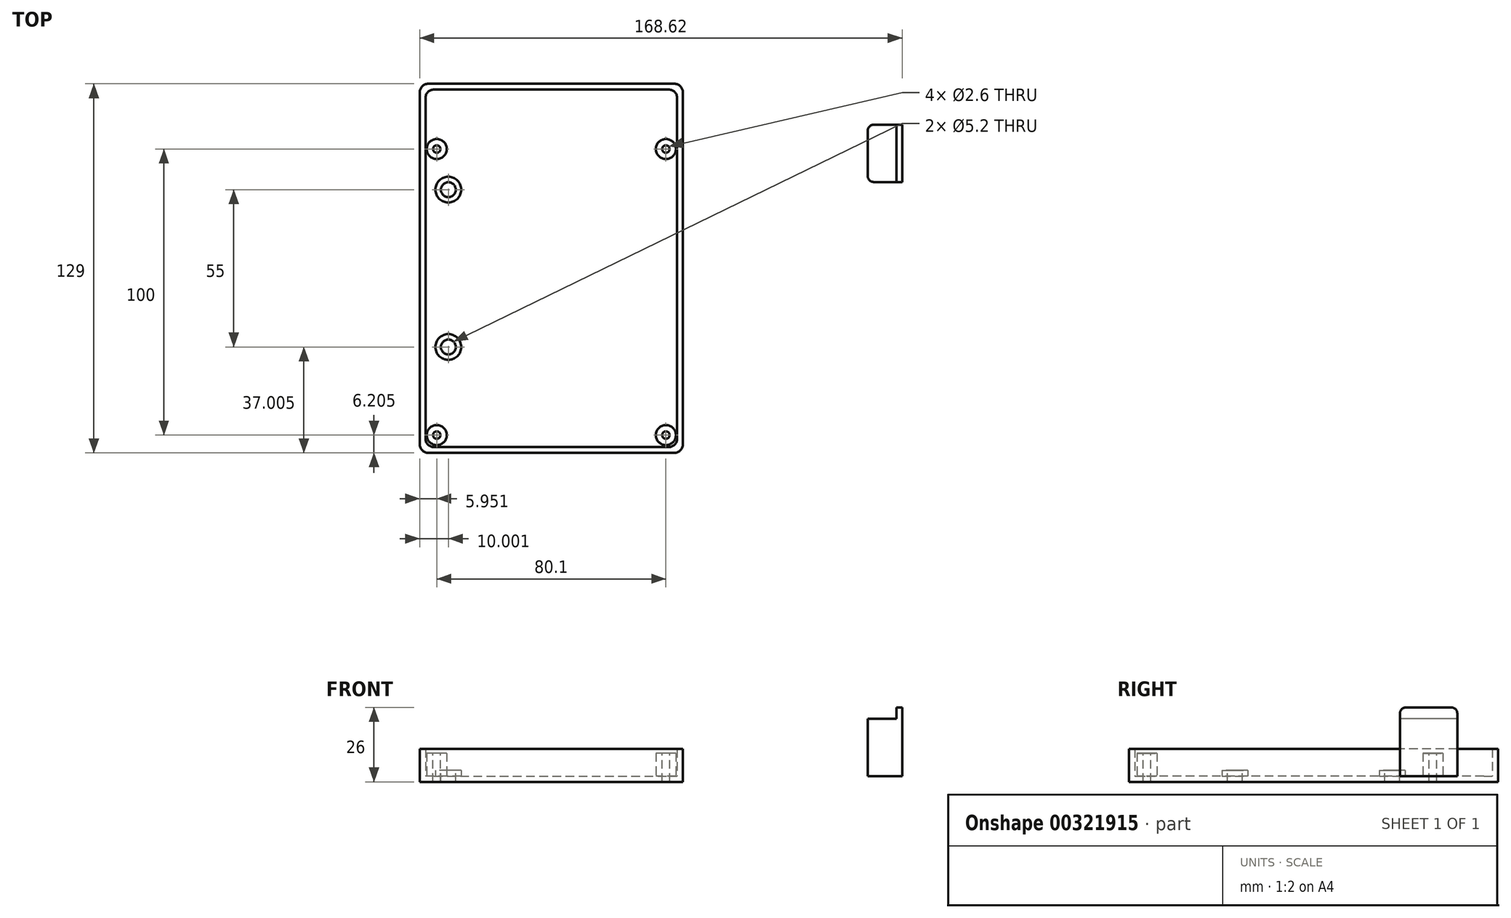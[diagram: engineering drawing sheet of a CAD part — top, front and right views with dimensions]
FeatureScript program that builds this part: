
annotation { "Feature Type Name" : "Feature", "Feature Type Description" : "" }
export const myFeature = defineFeature(function(context is Context, id is Id, definition is map)
    precondition{}
    {
        {
            var Q0;
            Q0=qCreatedBy(makeId("Top.planeOp"),FACE);
            var sketch = newSketch(context, id + "F0", { "sketchPlane" : qUnion([Q0])});
            skLineSegment(sketch, "E0.bottom", {"start": v(-100.3, 66.42) * mm, "end": v(-12.3, 66.42) * mm});
            skLineSegment(sketch, "E0.top", {"start": v(-100.3, -58.58) * mm, "end": v(-12.3, -58.58) * mm});
            skLineSegment(sketch, "E0.left", {"start": v(-100.3, 66.42) * mm, "end": v(-100.3, -58.58) * mm});
            skLineSegment(sketch, "E0.right", {"start": v(-12.3, 66.42) * mm, "end": v(-12.3, -58.58) * mm});
            skLineSegment(sketch, "E1.bottom", {"start": v(-102.3, 68.42) * mm, "end": v(-10.3, 68.42) * mm});
            skLineSegment(sketch, "E1.top", {"start": v(-102.3, -60.58) * mm, "end": v(-10.3, -60.58) * mm});
            skLineSegment(sketch, "E1.left", {"start": v(-102.3, 68.42) * mm, "end": v(-102.3, -60.58) * mm});
            skLineSegment(sketch, "E1.right", {"start": v(-10.3, 68.42) * mm, "end": v(-10.3, -60.58) * mm});
            skCircle(sketch, "E2", {"center": v(-16.25, 45.62) * mm, "radius": 1.3 * mm});
            skCircle(sketch, "E3", {"center": v(-16.25, -54.38) * mm, "radius": 1.3 * mm});
            skCircle(sketch, "E4", {"center": v(-96.35, -54.38) * mm, "radius": 1.3 * mm});
            skCircle(sketch, "E5", {"center": v(-96.35, 45.62) * mm, "radius": 1.3 * mm});
            skCircle(sketch, "E6", {"center": v(-16.25, 45.62) * mm, "radius": 3.5 * mm});
            skCircle(sketch, "E7", {"center": v(-16.25, -54.38) * mm, "radius": 3.5 * mm});
            skCircle(sketch, "E8", {"center": v(-96.35, -54.38) * mm, "radius": 3.5 * mm});
            skCircle(sketch, "E9", {"center": v(-96.35, 45.62) * mm, "radius": 3.5 * mm});
            skCircle(sketch, "E10", {"center": v(-92.3, 31.42) * mm, "radius": 2.6 * mm});
            skCircle(sketch, "E11", {"center": v(-92.3, -23.58) * mm, "radius": 2.6 * mm});
            skCircle(sketch, "E12", {"center": v(-92.3, 31.42) * mm, "radius": 4.5 * mm});
            skCircle(sketch, "E13", {"center": v(-92.3, -23.58) * mm, "radius": 4.5 * mm});
            skSolve(sketch);
        }
        {
            var Q0;
            {var subQ6=sQuery(id+"F0.wireOp",EDGE,"E0.bottom");Q0=makeQuery(id+"F0.imprint","IMPRINT",FACE,{"disambiguationData":[TD([[makeQuery(id+"F0.imprint","IMPRINT",EDGE,{"derivedFrom":subQ6}),-1.0]])]});}
            var Q1;
            {var subQ4=sQuery(id+"F0.wireOp",EDGE,"E0.bottom");Q1=makeQuery(id+"F0.imprint","IMPRINT",FACE,{"disambiguationData":[TD([[makeQuery(id+"F0.imprint","IMPRINT",EDGE,{"derivedFrom":subQ4}),1.0]])]});}
            var Q2;
            Q2=makeQuery(id+"F0.imprint","IMPRINT",FACE,{"disambiguationData":[TD([[makeQuery(id+"F0.imprint","IMPRINT",EDGE,{"derivedFrom":sQuery(id+"F0.wireOp",EDGE,"E5")}),-1.0]])]});
            var Q3;
            Q3=makeQuery(id+"F0.imprint","IMPRINT",FACE,{"disambiguationData":[TD([[makeQuery(id+"F0.imprint","IMPRINT",EDGE,{"derivedFrom":sQuery(id+"F0.wireOp",EDGE,"E4")}),-1.0]])]});
            var Q4;
            Q4=makeQuery(id+"F0.imprint","IMPRINT",FACE,{"disambiguationData":[TD([[makeQuery(id+"F0.imprint","IMPRINT",EDGE,{"derivedFrom":sQuery(id+"F0.wireOp",EDGE,"E3")}),-1.0]])]});
            var Q5;
            Q5=makeQuery(id+"F0.imprint","IMPRINT",FACE,{"disambiguationData":[TD([[makeQuery(id+"F0.imprint","IMPRINT",EDGE,{"derivedFrom":sQuery(id+"F0.wireOp",EDGE,"E2")}),-1.0]])]});
            var Q6;
            Q6=makeQuery(id+"F0.imprint","IMPRINT",FACE,{"disambiguationData":[TD([[makeQuery(id+"F0.imprint","IMPRINT",EDGE,{"derivedFrom":sQuery(id+"F0.wireOp",EDGE,"E10")}),-1.0]])]});
            var Q7;
            Q7=makeQuery(id+"F0.imprint","IMPRINT",FACE,{"disambiguationData":[TD([[makeQuery(id+"F0.imprint","IMPRINT",EDGE,{"derivedFrom":sQuery(id+"F0.wireOp",EDGE,"E11")}),-1.0]])]});
            extrude(context, id + "F1", {"entities" : qUnion([Q0, Q1, Q2, Q3, Q4, Q5, Q6, Q7]), "oppositeDirection" : true, "depth" : 2 * mm, "offsetDistance" : 25 * mm});
        }
        {
            var Q0;
            {var subQ4=sQuery(id+"F0.wireOp",EDGE,"E0.bottom");Q0=makeQuery(id+"F0.imprint","IMPRINT",FACE,{"disambiguationData":[TD([[makeQuery(id+"F0.imprint","IMPRINT",EDGE,{"derivedFrom":subQ4}),1.0]])]});}
            extrude(context, id + "F2", {"entities" : qUnion([Q0]), "operationType" : NewBodyOperationType.ADD, "depth" : 9.5 * mm, "offsetDistance" : 25 * mm});
        }
        {
            var Q0;
            Q0=makeQuery(id+"F0.imprint","IMPRINT",FACE,{"disambiguationData":[TD([[makeQuery(id+"F0.imprint","IMPRINT",EDGE,{"derivedFrom":sQuery(id+"F0.wireOp",EDGE,"E10")}),-1.0]])]});
            var Q1;
            Q1=makeQuery(id+"F0.imprint","IMPRINT",FACE,{"disambiguationData":[TD([[makeQuery(id+"F0.imprint","IMPRINT",EDGE,{"derivedFrom":sQuery(id+"F0.wireOp",EDGE,"E11")}),-1.0]])]});
            extrude(context, id + "F3", {"entities" : qUnion([Q0, Q1]), "operationType" : NewBodyOperationType.ADD, "depth" : 2 * mm, "offsetDistance" : 25 * mm});
        }
        {
            var Q0;
            Q0=makeQuery(id+"F0.imprint","IMPRINT",FACE,{"disambiguationData":[TD([[makeQuery(id+"F0.imprint","IMPRINT",EDGE,{"derivedFrom":sQuery(id+"F0.wireOp",EDGE,"E5")}),-1.0]])]});
            var Q1;
            Q1=makeQuery(id+"F0.imprint","IMPRINT",FACE,{"disambiguationData":[TD([[makeQuery(id+"F0.imprint","IMPRINT",EDGE,{"derivedFrom":sQuery(id+"F0.wireOp",EDGE,"E4")}),-1.0]])]});
            var Q2;
            Q2=makeQuery(id+"F0.imprint","IMPRINT",FACE,{"disambiguationData":[TD([[makeQuery(id+"F0.imprint","IMPRINT",EDGE,{"derivedFrom":sQuery(id+"F0.wireOp",EDGE,"E2")}),-1.0]])]});
            var Q3;
            Q3=makeQuery(id+"F0.imprint","IMPRINT",FACE,{"disambiguationData":[TD([[makeQuery(id+"F0.imprint","IMPRINT",EDGE,{"derivedFrom":sQuery(id+"F0.wireOp",EDGE,"E3")}),-1.0]])]});
            extrude(context, id + "F4", {"entities" : qUnion([Q0, Q1, Q2, Q3]), "operationType" : NewBodyOperationType.ADD, "depth" : 8 * mm, "offsetDistance" : 25 * mm});
        }
        {
            var Q0;
            Q0=makeQuery(id+"F2.opExtrude","SWEPT_EDGE",EDGE,{"disambiguationData":[OSD([sQuery(id+"F0.wireOp",EDGE,"E0.bottom"),sQuery(id+"F0.wireOp",EDGE,"E0.left")])]});
            var Q1;
            Q1=makeQuery(id+"F2.opExtrude","SWEPT_EDGE",EDGE,{"disambiguationData":[OSD([sQuery(id+"F0.wireOp",EDGE,"E0.bottom"),sQuery(id+"F0.wireOp",EDGE,"E0.right")])]});
            var Q2;
            Q2=makeQuery(id+"F2.opExtrude","SWEPT_EDGE",EDGE,{"disambiguationData":[OSD([sQuery(id+"F0.wireOp",EDGE,"E0.top"),sQuery(id+"F0.wireOp",EDGE,"E0.left")])]});
            var Q3;
            Q3=makeQuery(id+"F2.opExtrude","SWEPT_EDGE",EDGE,{"disambiguationData":[OSD([sQuery(id+"F0.wireOp",EDGE,"E0.top"),sQuery(id+"F0.wireOp",EDGE,"E0.right")])]});
            var Q4;
            {var subQ0=sQuery(id+"F0.wireOp",EDGE,"E1.right");var subQ1=sQuery(id+"F0.wireOp",EDGE,"E1.bottom");Q4=makeQuery(id+"F2.boolean.opBoolean","MERGE",EDGE,{"derivedFrom":[makeQuery(id+"F1.opExtrude","SWEPT_EDGE",EDGE,{"disambiguationData":[OSD([subQ1,subQ0])]}),makeQuery(id+"F2.opExtrude","SWEPT_EDGE",EDGE,{"disambiguationData":[OSD([subQ1,subQ0])]})]});}
            var Q5;
            {var subQ0=sQuery(id+"F0.wireOp",EDGE,"E1.left");var subQ1=sQuery(id+"F0.wireOp",EDGE,"E1.bottom");Q5=makeQuery(id+"F2.boolean.opBoolean","MERGE",EDGE,{"derivedFrom":[makeQuery(id+"F1.opExtrude","SWEPT_EDGE",EDGE,{"disambiguationData":[OSD([subQ1,subQ0])]}),makeQuery(id+"F2.opExtrude","SWEPT_EDGE",EDGE,{"disambiguationData":[OSD([subQ1,subQ0])]})]});}
            var Q6;
            {var subQ0=sQuery(id+"F0.wireOp",EDGE,"E1.right");var subQ1=sQuery(id+"F0.wireOp",EDGE,"E1.top");Q6=makeQuery(id+"F2.boolean.opBoolean","MERGE",EDGE,{"derivedFrom":[makeQuery(id+"F1.opExtrude","SWEPT_EDGE",EDGE,{"disambiguationData":[OSD([subQ1,subQ0])]}),makeQuery(id+"F2.opExtrude","SWEPT_EDGE",EDGE,{"disambiguationData":[OSD([subQ1,subQ0])]})]});}
            var Q7;
            {var subQ0=sQuery(id+"F0.wireOp",EDGE,"E1.left");var subQ1=sQuery(id+"F0.wireOp",EDGE,"E1.top");Q7=makeQuery(id+"F2.boolean.opBoolean","MERGE",EDGE,{"derivedFrom":[makeQuery(id+"F1.opExtrude","SWEPT_EDGE",EDGE,{"disambiguationData":[OSD([subQ1,subQ0])]}),makeQuery(id+"F2.opExtrude","SWEPT_EDGE",EDGE,{"disambiguationData":[OSD([subQ1,subQ0])]})]});}
            fillet(context, id + "F5", {"entities" : qUnion([Q0, Q1, Q2, Q3, Q4, Q5, Q6, Q7]), "radius" : 3 * mm, "tangentPropagation" : true, "allowEdgeOverflow" : false});
        }
        {
            var Q0;
            Q0=qCreatedBy(makeId("Top.planeOp"),FACE);
            var sketch = newSketch(context, id + "F6", { "sketchPlane" : qUnion([Q0])});
            skLineSegment(sketch, "E14.bottom", {"start": v(54.32, 54.11) * mm, "end": v(66.32, 54.11) * mm});
            skLineSegment(sketch, "E14.top", {"start": v(54.32, 34.11) * mm, "end": v(66.32, 34.11) * mm});
            skLineSegment(sketch, "E14.left", {"start": v(54.32, 54.11) * mm, "end": v(54.32, 34.11) * mm});
            skLineSegment(sketch, "E14.right", {"start": v(66.32, 54.11) * mm, "end": v(66.32, 34.11) * mm});
            skSolve(sketch);
        }
        {
            var Q0;
            Q0=makeQuery(id+"F6.imprint","IMPRINT",FACE,{"disambiguationData":[TD([[makeQuery(id+"F6.imprint","IMPRINT",EDGE,{"derivedFrom":sQuery(id+"F6.wireOp",EDGE,"E14.bottom")}),-1.0]])]});
            extrude(context, id + "F7", {"entities" : qUnion([Q0]), "depth" : 24 * mm, "offsetDistance" : 25 * mm});
        }
        {
            var Q0;
            Q0=makeQuery(id+"F7.opExtrude","CAP_FACE",FACE,{"disambiguationData":[OSD([sQuery(id+"F6.wireOp",EDGE,"E14.bottom"),sQuery(id+"F6.wireOp",EDGE,"E14.top"),sQuery(id+"F6.wireOp",EDGE,"E14.left"),sQuery(id+"F6.wireOp",EDGE,"E14.right")])],"isStart":false});
            var sketch = newSketch(context, id + "F8", { "sketchPlane" : qUnion([Q0])});
            skLineSegment(sketch, "E15", {"start": v(64.32, 54.11) * mm, "end": v(64.32, 34.11) * mm});
            skSolve(sketch);
        }
        {
            var Q0;
            {var subQ0=sQuery(id+"F8.wireOp",EDGE,"E15");Q0=makeQuery(id+"F8.imprint","IMPRINT",FACE,{"disambiguationData":[TD([[makeQuery(id+"F8.imprint","IMPRINT",EDGE,{"derivedFrom":subQ0}),-1.0]])]});}
            extrude(context, id + "F9", {"entities" : qUnion([Q0]), "operationType" : NewBodyOperationType.REMOVE, "oppositeDirection" : true, "depth" : 4 * mm, "offsetDistance" : 25 * mm});
        }
        {
            var Q0;
            Q0=makeQuery(id+"F7.opExtrude","CAP_EDGE",EDGE,{"disambiguationData":[OSD([sQuery(id+"F6.wireOp",EDGE,"E14.top")])],"isStart":false});
            var Q1;
            Q1=makeQuery(id+"F7.opExtrude","CAP_EDGE",EDGE,{"disambiguationData":[OSD([sQuery(id+"F6.wireOp",EDGE,"E14.bottom")])],"isStart":false});
            var Q2;
            Q2=makeQuery(id+"F7.opExtrude","SWEPT_EDGE",EDGE,{"disambiguationData":[OSD([sQuery(id+"F6.wireOp",EDGE,"E14.top"),sQuery(id+"F6.wireOp",EDGE,"E14.left")])]});
            var Q3;
            Q3=makeQuery(id+"F7.opExtrude","SWEPT_EDGE",EDGE,{"disambiguationData":[OSD([sQuery(id+"F6.wireOp",EDGE,"E14.bottom"),sQuery(id+"F6.wireOp",EDGE,"E14.left")])]});
            fillet(context, id + "F10", {"entities" : qUnion([Q0, Q1, Q2, Q3]), "radius" : 2 * mm, "tangentPropagation" : true, "allowEdgeOverflow" : false});
        }
    });
